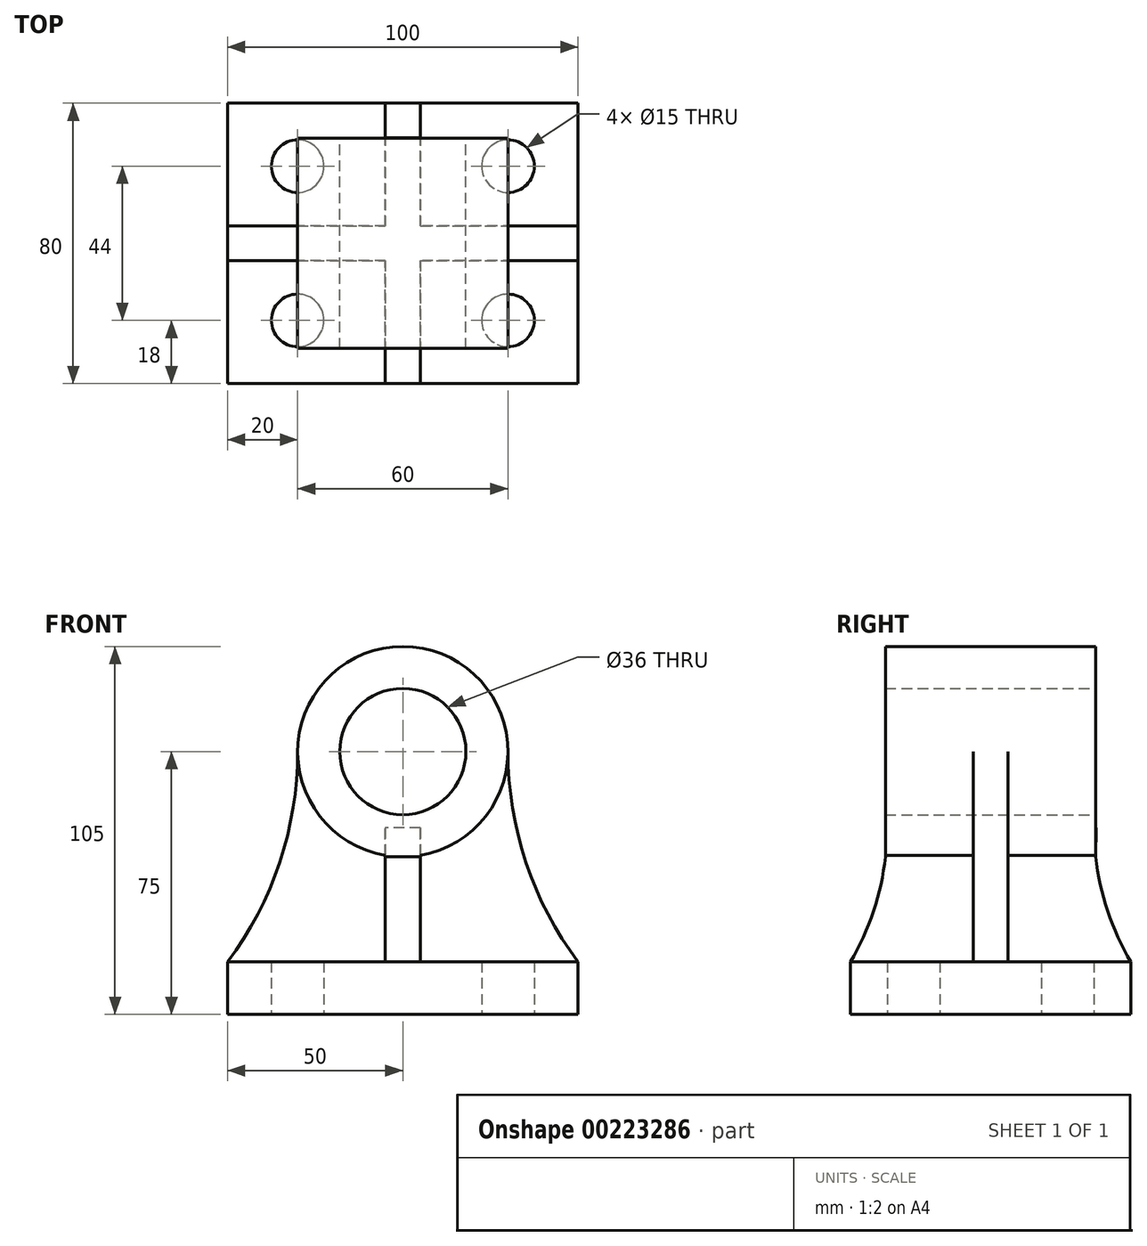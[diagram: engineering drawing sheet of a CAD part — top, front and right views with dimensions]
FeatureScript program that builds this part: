
annotation { "Feature Type Name" : "Feature", "Feature Type Description" : "" }
export const myFeature = defineFeature(function(context is Context, id is Id, definition is map)
    precondition{}
    {
        {
            var Q0;
            Q0=qCreatedBy(makeId("Front.planeOp"),FACE);
            var sketch = newSketch(context, id + "F0", { "sketchPlane" : qUnion([Q0])});
            skLineSegment(sketch, "E0", {"start": v(0, 0) * mm, "end": v(100, 0) * mm});
            skLineSegment(sketch, "E1", {"start": v(100, 0) * mm, "end": v(100, 15) * mm});
            skLineSegment(sketch, "E2", {"start": v(100, 15) * mm, "end": v(0, 15) * mm});
            skLineSegment(sketch, "E3", {"start": v(0, 15) * mm, "end": v(0, 0) * mm});
            skLineSegment(sketch, "E4", {"start": v(50, 98.8) * mm, "end": v(50, -59.3) * mm, "construction": true});
            skLineSegment(sketch, "E5", {"start": v(-16.96, 75) * mm, "end": v(141.13, 75) * mm, "construction": true});
            skCircle(sketch, "E6", {"center": v(50, 75) * mm, "radius": 30 * mm});
            skCircle(sketch, "E7", {"center": v(50, 75) * mm, "radius": 18 * mm});
            skArc(sketch, "E8", {"start": v(0, 15) * mm, "mid": v(14.87, 43.38) * mm, "end": v(20, 75) * mm});
            skArc(sketch, "E9", {"start": v(80, 75) * mm, "mid": v(85.13, 43.38) * mm, "end": v(100, 15) * mm});
            skSolve(sketch);
        }
        {
            var Q0;
            Q0=makeQuery(id+"F0.imprint","IMPRINT",FACE,{"disambiguationData":[TD([[makeQuery(id+"F0.imprint","IMPRINT",EDGE,{"derivedFrom":sQuery(id+"F0.wireOp",EDGE,"E0")}),1.0]])]});
            extrude(context, id + "F1", {"entities" : qUnion([Q0]), "endBound" : BoundingType.SYMMETRIC, "depth" : 80 * mm});
        }
        {
            var Q0;
            Q0=makeQuery(id+"F0.imprint","IMPRINT",FACE,{"disambiguationData":[TD([[makeQuery(id+"F0.imprint","IMPRINT",EDGE,{"derivedFrom":sQuery(id+"F0.wireOp",EDGE,"E7")}),-1.0]])]});
            extrude(context, id + "F2", {"entities" : qUnion([Q0]), "operationType" : NewBodyOperationType.ADD, "endBound" : BoundingType.SYMMETRIC, "depth" : 60 * mm});
        }
        {
            var Q0;
            Q0=makeQuery(id+"F0.imprint","IMPRINT",FACE,{"disambiguationData":[TD([[makeQuery(id+"F0.imprint","IMPRINT",EDGE,{"derivedFrom":sQuery(id+"F0.wireOp",EDGE,"E2")}),-1.0]])]});
            extrude(context, id + "F3", {"entities" : qUnion([Q0]), "operationType" : NewBodyOperationType.ADD, "endBound" : BoundingType.SYMMETRIC, "depth" : 10 * mm});
        }
        {
            var Q0;
            Q0=qCreatedBy(makeId("Right.planeOp"),FACE);
            cPlane(context, id + "F4", {"entities" : qUnion([Q0]), "cplaneType" : CPlaneType.OFFSET, "offset" : 45 * mm, "width" : 150 * mm, "height" : 150 * mm});
        }
        {
            var Q0;
            Q0=qCreatedBy(id+"F4.planeOp",FACE);
            var sketch = newSketch(context, id + "F5", { "sketchPlane" : qUnion([Q0])});
            skArc(sketch, "E10", {"start": v(30, 45) * mm, "mid": v(33.4, 29.47) * mm, "end": v(40, 15) * mm});
            skArc(sketch, "E11", {"start": v(-40, 15) * mm, "mid": v(-33.4, 29.47) * mm, "end": v(-30, 45) * mm});
            skLineSegment(sketch, "E12", {"start": v(5, 45) * mm, "end": v(-5, 45) * mm});
            skLineSegment(sketch, "E13.0", {"start": v(5, 15) * mm, "end": v(40, 15) * mm});
            skLineSegment(sketch, "E14.0", {"start": v(-40, 15) * mm, "end": v(-5, 15) * mm});
            skLineSegment(sketch, "E15", {"start": v(5, 15) * mm, "end": v(-5, 15) * mm});
            skLineSegment(sketch, "E16", {"start": v(-5, 45) * mm, "end": v(5, 45) * mm});
            skLineSegment(sketch, "E17", {"start": v(-30, 45) * mm, "end": v(-30, 53.22) * mm});
            skLineSegment(sketch, "E18", {"start": v(-30, 53.22) * mm, "end": v(30.08, 53.22) * mm});
            skLineSegment(sketch, "E19", {"start": v(30.08, 53.22) * mm, "end": v(30, 45) * mm});
            skSolve(sketch);
        }
        {
            var Q0;
            Q0=makeQuery(id+"F5.imprint","IMPRINT",FACE,{"disambiguationData":[TD([[makeQuery(id+"F5.imprint","IMPRINT",EDGE,{"derivedFrom":sQuery(id+"F5.wireOp",EDGE,"E10")}),-1.0]])]});
            extrude(context, id + "F6", {"entities" : qUnion([Q0]), "operationType" : NewBodyOperationType.ADD, "depth" : 10 * mm});
        }
        {
            var Q0;
            Q0=makeQuery(id+"F1.opExtrude","SWEPT_FACE",FACE,{"disambiguationData":[OSD([sQuery(id+"F0.wireOp",EDGE,"E0")])]});
            var sketch = newSketch(context, id + "F7", { "sketchPlane" : qUnion([Q0])});
            skCircle(sketch, "E20", {"center": v(80, -22) * mm, "radius": 7.5 * mm});
            skCircle(sketch, "E21", {"center": v(20, -22) * mm, "radius": 7.5 * mm});
            skCircle(sketch, "E22", {"center": v(80, 22) * mm, "radius": 7.5 * mm});
            skCircle(sketch, "E23", {"center": v(20, 22) * mm, "radius": 7.5 * mm});
            skLineSegment(sketch, "E24.0.0", {"start": v(0, -40) * mm, "end": v(100, -40) * mm});
            skLineSegment(sketch, "E24.0.1", {"start": v(100, -40) * mm, "end": v(100, 40) * mm});
            skLineSegment(sketch, "E24.0.2", {"start": v(100, 40) * mm, "end": v(0, 40) * mm});
            skLineSegment(sketch, "E24.0.3", {"start": v(0, 40) * mm, "end": v(0, -40) * mm});
            skSolve(sketch);
        }
        {
            var Q0;
            Q0=makeQuery(id+"F7.imprint","IMPRINT",FACE,{"disambiguationData":[TD([[makeQuery(id+"F7.imprint","IMPRINT",EDGE,{"derivedFrom":sQuery(id+"F7.wireOp",EDGE,"E20")}),1.0]])]});
            var Q1;
            Q1=makeQuery(id+"F7.imprint","IMPRINT",FACE,{"disambiguationData":[TD([[makeQuery(id+"F7.imprint","IMPRINT",EDGE,{"derivedFrom":sQuery(id+"F7.wireOp",EDGE,"E21")}),1.0]])]});
            var Q2;
            Q2=makeQuery(id+"F7.imprint","IMPRINT",FACE,{"disambiguationData":[TD([[makeQuery(id+"F7.imprint","IMPRINT",EDGE,{"derivedFrom":sQuery(id+"F7.wireOp",EDGE,"E22")}),1.0]])]});
            var Q3;
            Q3=makeQuery(id+"F7.imprint","IMPRINT",FACE,{"disambiguationData":[TD([[makeQuery(id+"F7.imprint","IMPRINT",EDGE,{"derivedFrom":sQuery(id+"F7.wireOp",EDGE,"E23")}),1.0]])]});
            extrude(context, id + "F8", {"entities" : qUnion([Q0, Q1, Q2, Q3]), "operationType" : NewBodyOperationType.REMOVE, "endBound" : BoundingType.UP_TO_NEXT, "oppositeDirection" : true, "depth" : 25 * mm});
        }
    });
